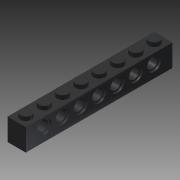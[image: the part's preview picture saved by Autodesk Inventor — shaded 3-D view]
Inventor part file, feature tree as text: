
AUTODESK INVENTOR PART (.ipt)
format: ipt  version: 2013 (Build 170138000, 138)  size: 189,952 bytes
history: native  units: mm
features: extrude x5, sketch x2, pattern_linear x2, plane x1, mirror x1
ambient origin geometry x8: Origin, YZ Plane, XZ Plane, XY Plane, X Axis, Y Axis, Z Axis, Center Point
bodies: Solid1 (feature_tree)
feature tree (11):
  sketch  "Sketch1"  dims[d0=8.0mm d1=8.0mm]
  extrude  "Extrusion1"  Depth=8.0mm
  extrude  "Extrusion2"  Depth=9.6mm TaperAngle=0.0deg
  extrude  "Extrusion3"  Depth=11.3mm TaperAngle=0.0deg
  pattern_linear  "Rectangular Pattern1"  Spacing1=1.7mm  [1 undecoded]
  sketch  "Sketch2"  dims[d2=4.8mm d3=9.6mm d4=0.0mm d5=11.3mm d6=0.0mm d7=1.7mm d8=0.0mm d9=80.0mm d11=8.0mm d12=4.8mm d14=6.2mm d15=1.7mm d16=0.0mm d17=0.8mm d18=0.0mm d19=70.0mm d21=8.0mm d22=8.0mm d23=5.6mm]
  plane  "Work Plane1"
  extrude  "Extrusion4"  Depth=80.0mm
  extrude  "Extrusion5"  Depth=4.8mm
  mirror  "Mirror1"
  pattern_linear  "Rectangular Pattern2"  Spacing1=6.2mm  [1 undecoded]
note: 2 required parameter values undecoded (feature->parameter linkage not recoverable at this tier; creation-order binding heuristic only, values carry confidence <= 0.55)
